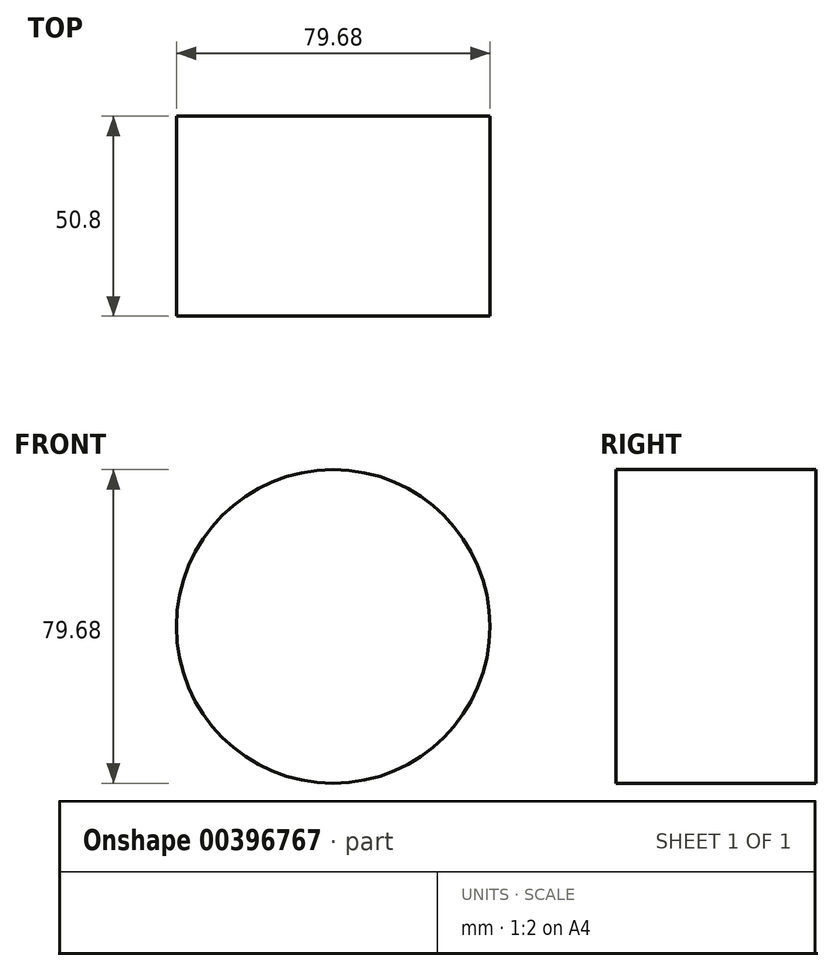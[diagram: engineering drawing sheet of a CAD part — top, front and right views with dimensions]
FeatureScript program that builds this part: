
annotation { "Feature Type Name" : "Feature", "Feature Type Description" : "" }
export const myFeature = defineFeature(function(context is Context, id is Id, definition is map)
    precondition{}
    {
        {
            var Q0;
            Q0=qCreatedBy(makeId("Front.planeOp"),FACE);
            var sketch = newSketch(context, id + "F0", { "sketchPlane" : qUnion([Q0])});
            skCircle(sketch, "E0", {"center": v(0, 0) * mm, "radius": 39.84 * mm});
            skSolve(sketch);
        }
        {
            var Q0;
            Q0 = qSketchRegion(id + "F0", true);
            extrude(context, id + "F1", {"entities" : qUnion([Q0]), "depth" : 25.4 * mm});
        }
        {
            var Q0;
            Q0=qCreatedBy(makeId("Top.planeOp"),FACE);
            var sketch = newSketch(context, id + "F2", { "sketchPlane" : qUnion([Q0])});
            skSolve(sketch);
        }
        {
            var Q0;
            Q0=makeQuery(id+"F1.opExtrude","CAP_FACE",FACE,{"disambiguationData":[OSD([sQuery(id+"F0.wireOp",EDGE,"E0")])],"isStart":false});
            var Q1;
            Q1=makeQuery(id+"F1.opExtrude","CAP_FACE",FACE,{"disambiguationData":[OSD([sQuery(id+"F0.wireOp",EDGE,"E0")])],"isStart":true});
            var Q2;
            Q2 = qSketchRegion(id + "F2", true);
            extrude(context, id + "F3", {"entities" : qUnion([Q0, Q1, Q2]), "operationType" : NewBodyOperationType.ADD, "depth" : 25.4 * mm});
        }
    });
